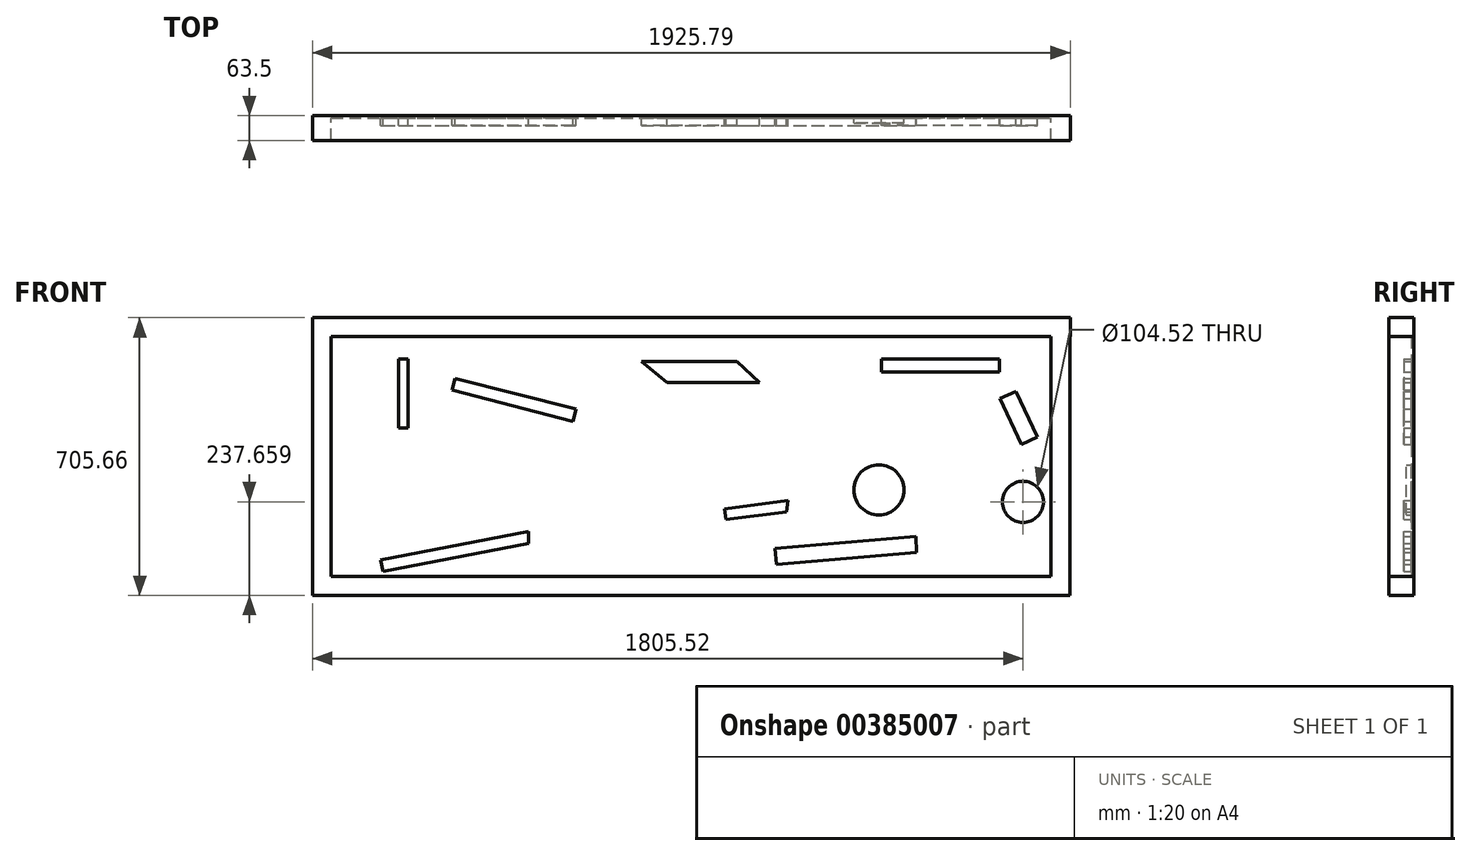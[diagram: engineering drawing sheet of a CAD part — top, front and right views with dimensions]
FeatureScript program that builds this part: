
annotation { "Feature Type Name" : "Feature", "Feature Type Description" : "" }
export const myFeature = defineFeature(function(context is Context, id is Id, definition is map)
    precondition{}
    {
        {
            var Q0;
            Q0=qCreatedBy(makeId("Front.planeOp"),FACE);
            var sketch = newSketch(context, id + "F0", { "sketchPlane" : qUnion([Q0])});
            skLineSegment(sketch, "E0.bottom", {"start": v(-921.13, 198.65) * mm, "end": v(907.67, 198.65) * mm});
            skLineSegment(sketch, "E0.top", {"start": v(-921.13, -410.95) * mm, "end": v(907.67, -410.95) * mm});
            skLineSegment(sketch, "E0.left", {"start": v(-921.13, 198.65) * mm, "end": v(-921.13, -410.95) * mm});
            skLineSegment(sketch, "E0.right", {"start": v(907.67, 198.65) * mm, "end": v(907.67, -410.95) * mm});
            skCircle(sketch, "E1", {"center": v(836.35, -221.32) * mm, "radius": 52.26 * mm});
            skLineSegment(sketch, "E2.bottom", {"start": v(-749.92, 141.95) * mm, "end": v(-725.7, 141.95) * mm});
            skLineSegment(sketch, "E2.top", {"start": v(-749.92, -33.63) * mm, "end": v(-725.7, -33.63) * mm});
            skLineSegment(sketch, "E2.left", {"start": v(-749.92, 141.95) * mm, "end": v(-749.92, -33.63) * mm});
            skLineSegment(sketch, "E2.right", {"start": v(-725.7, 141.95) * mm, "end": v(-725.7, -33.63) * mm});
            skLineSegment(sketch, "E3.bottom", {"start": v(775.8, 141.95) * mm, "end": v(476.1, 141.95) * mm});
            skLineSegment(sketch, "E3.top", {"start": v(775.8, 108.65) * mm, "end": v(476.1, 108.65) * mm});
            skLineSegment(sketch, "E3.left", {"start": v(775.8, 141.95) * mm, "end": v(775.8, 108.65) * mm});
            skLineSegment(sketch, "E3.right", {"start": v(476.1, 141.95) * mm, "end": v(476.1, 108.65) * mm});
            skLineSegment(sketch, "E4", {"start": v(206.69, -339.38) * mm, "end": v(563.9, -309.11) * mm});
            skLineSegment(sketch, "E5", {"start": v(206.69, -339.38) * mm, "end": v(210.17, -380.5) * mm});
            skLineSegment(sketch, "E6", {"start": v(210.17, -380.5) * mm, "end": v(566.06, -350.33) * mm});
            skLineSegment(sketch, "E7", {"start": v(566.06, -350.33) * mm, "end": v(563.9, -309.11) * mm});
            skLineSegment(sketch, "E8", {"start": v(109.81, 135.9) * mm, "end": v(-132.36, 135.9) * mm});
            skLineSegment(sketch, "E9", {"start": v(109.81, 135.9) * mm, "end": v(167.33, 81.4) * mm});
            skLineSegment(sketch, "E10", {"start": v(-132.36, 135.9) * mm, "end": v(-68.8, 81.4) * mm});
            skLineSegment(sketch, "E11", {"start": v(-68.8, 81.4) * mm, "end": v(167.33, 81.4) * mm});
            skLineSegment(sketch, "E12.bottom", {"start": v(-921.13, 198.65) * mm, "end": v(-969.17, 198.65) * mm});
            skLineSegment(sketch, "E12.top", {"start": v(-921.13, -410.95) * mm, "end": v(-969.17, -410.95) * mm});
            skLineSegment(sketch, "E12.right", {"start": v(-969.17, 198.65) * mm, "end": v(-969.17, -410.95) * mm});
            skLineSegment(sketch, "E13.bottom", {"start": v(907.67, 198.65) * mm, "end": v(955.7, 198.65) * mm});
            skLineSegment(sketch, "E13.top", {"start": v(907.67, -410.95) * mm, "end": v(955.7, -410.95) * mm});
            skLineSegment(sketch, "E13.right", {"start": v(955.7, 198.65) * mm, "end": v(955.7, -410.95) * mm});
            skLineSegment(sketch, "E14.bottom", {"start": v(-969.17, -410.95) * mm, "end": v(955.7, -410.95) * mm});
            skLineSegment(sketch, "E15.bottom", {"start": v(-969.17, -410.95) * mm, "end": v(955.73, -410.95) * mm});
            skLineSegment(sketch, "E15.top", {"start": v(-969.17, -458.98) * mm, "end": v(955.73, -458.98) * mm});
            skLineSegment(sketch, "E15.left", {"start": v(-969.17, -410.95) * mm, "end": v(-969.17, -458.98) * mm});
            skLineSegment(sketch, "E15.right", {"start": v(955.73, -410.95) * mm, "end": v(955.73, -458.98) * mm});
            skLineSegment(sketch, "E16.bottom", {"start": v(-969.17, 198.65) * mm, "end": v(956.62, 198.65) * mm});
            skLineSegment(sketch, "E16.top", {"start": v(-969.17, 246.68) * mm, "end": v(956.62, 246.68) * mm});
            skLineSegment(sketch, "E16.left", {"start": v(-969.17, 198.65) * mm, "end": v(-969.17, 246.68) * mm});
            skLineSegment(sketch, "E16.right", {"start": v(956.62, 198.65) * mm, "end": v(956.62, 246.68) * mm});
            skLineSegment(sketch, "E17.bottom", {"start": v(-921.13, -410.95) * mm, "end": v(-31.47, -410.95) * mm});
            skLineSegment(sketch, "E17.left", {"start": v(-921.13, -410.95) * mm, "end": v(-921.13, -371.5) * mm});
            skLineSegment(sketch, "E18", {"start": v(-606.28, 91.49) * mm, "end": v(-299.2, 14.32) * mm});
            skLineSegment(sketch, "E19", {"start": v(-299.2, 14.32) * mm, "end": v(-307.1, -17.17) * mm});
            skLineSegment(sketch, "E20", {"start": v(-307.1, -17.17) * mm, "end": v(-614.07, 62.56) * mm});
            skLineSegment(sketch, "E21", {"start": v(-614.07, 62.56) * mm, "end": v(-606.28, 91.49) * mm});
            skLineSegment(sketch, "E22", {"start": v(81.92, -266.64) * mm, "end": v(235.6, -246.6) * mm});
            skLineSegment(sketch, "E23", {"start": v(81.92, -266.64) * mm, "end": v(78.34, -239.22) * mm});
            skLineSegment(sketch, "E24", {"start": v(78.34, -239.22) * mm, "end": v(239.82, -218.16) * mm});
            skLineSegment(sketch, "E25", {"start": v(239.82, -218.16) * mm, "end": v(235.6, -246.6) * mm});
            skLineSegment(sketch, "E26", {"start": v(-795.26, -368.88) * mm, "end": v(-420.46, -296.43) * mm});
            skLineSegment(sketch, "E27", {"start": v(-795.26, -368.88) * mm, "end": v(-789.58, -398.26) * mm});
            skLineSegment(sketch, "E28", {"start": v(-789.58, -398.26) * mm, "end": v(-420.46, -326.9) * mm});
            skLineSegment(sketch, "E29", {"start": v(-420.46, -326.9) * mm, "end": v(-420.46, -296.43) * mm});
            skLineSegment(sketch, "E30", {"start": v(818.66, 58.8) * mm, "end": v(872.92, -56.8) * mm});
            skLineSegment(sketch, "E31", {"start": v(872.92, -56.8) * mm, "end": v(832.51, -75.76) * mm});
            skLineSegment(sketch, "E32", {"start": v(832.51, -75.76) * mm, "end": v(777.59, 41.28) * mm});
            skLineSegment(sketch, "E33", {"start": v(777.59, 41.28) * mm, "end": v(818.66, 58.8) * mm});
            skCircle(sketch, "E34", {"center": v(470.15, -190.9) * mm, "radius": 63.63 * mm});
            skSolve(sketch);
        }
        {
            var Q0;
            Q0=makeQuery(id+"F0.imprint","IMPRINT",FACE,{"disambiguationData":[TD([[makeQuery(id+"F0.imprint","IMPRINT",EDGE,{"derivedFrom":sQuery(id+"F0.wireOp",EDGE,"E16.top")}),-1.0]])]});
            var Q1;
            {var subQ0=sQuery(id+"F0.wireOp",EDGE,"E12.right");Q1=makeQuery(id+"F0.imprint","IMPRINT",FACE,{"disambiguationData":[TD([[makeQuery(id+"F0.imprint","IMPRINT",EDGE,{"derivedFrom":subQ0}),1.0]])]});}
            var Q2;
            Q2=makeQuery(id+"F0.imprint","IMPRINT",FACE,{"disambiguationData":[TD([[makeQuery(id+"F0.imprint","IMPRINT",EDGE,{"derivedFrom":sQuery(id+"F0.wireOp",EDGE,"E15.top")}),1.0]])]});
            var Q3;
            {var subQ0=sQuery(id+"F0.wireOp",EDGE,"E13.right");Q3=makeQuery(id+"F0.imprint","IMPRINT",FACE,{"disambiguationData":[TD([[makeQuery(id+"F0.imprint","IMPRINT",EDGE,{"derivedFrom":subQ0}),-1.0]])]});}
            extrude(context, id + "F1", {"entities" : qUnion([Q0, Q1, Q2, Q3]), "depth" : 63.5 * mm});
        }
        {
            var Q0;
            {var subQ0=sQuery(id+"F0.wireOp",EDGE,"E0.top");Q0=makeQuery(id+"F0.imprint","IMPRINT",FACE,{"disambiguationData":[TD([[makeQuery(id+"F0.imprint","IMPRINT",EDGE,{"derivedFrom":subQ0}),1.0]])]});}
            extrude(context, id + "F2", {"entities" : qUnion([Q0]), "operationType" : NewBodyOperationType.ADD, "depth" : 6.35 * mm});
        }
        {
            var Q0;
            Q0=qCreatedBy(makeId("Right.planeOp"),FACE);
            var sketch = newSketch(context, id + "F3", { "sketchPlane" : qUnion([Q0])});
            skArc(sketch, "E35", {"start": v(0, 0) * mm, "mid": v(-49.1, -67.34) * mm, "end": v(0, -134.69) * mm});
            skSolve(sketch);
        }
        {
            var Q0;
            Q0=sQuery(id+"F3.wireOp",EDGE,"E35");
            extrude(context, id + "F4", {"bodyType" : ToolBodyType.SURFACE, "surfaceEntities" : qUnion([Q0]), "depth" : 152.4 * mm, "hasSecondDirection" : true, "secondDirectionOppositeDirection" : true, "secondDirectionDepth" : 177.8 * mm});
        }
        {
            var Q0;
            Q0=makeQuery(id+"F0.imprint","IMPRINT",FACE,{"disambiguationData":[TD([[makeQuery(id+"F0.imprint","IMPRINT",EDGE,{"derivedFrom":sQuery(id+"F0.wireOp",EDGE,"E3.bottom")}),1.0]])]});
            var Q1;
            Q1=makeQuery(id+"F0.imprint","IMPRINT",FACE,{"disambiguationData":[TD([[makeQuery(id+"F0.imprint","IMPRINT",EDGE,{"derivedFrom":sQuery(id+"F0.wireOp",EDGE,"E8")}),1.0]])]});
            var Q2;
            Q2=makeQuery(id+"F0.imprint","IMPRINT",FACE,{"disambiguationData":[TD([[makeQuery(id+"F0.imprint","IMPRINT",EDGE,{"derivedFrom":sQuery(id+"F0.wireOp",EDGE,"E18")}),-1.0]])]});
            var Q3;
            Q3=makeQuery(id+"F0.imprint","IMPRINT",FACE,{"disambiguationData":[TD([[makeQuery(id+"F0.imprint","IMPRINT",EDGE,{"derivedFrom":sQuery(id+"F0.wireOp",EDGE,"E26")}),-1.0]])]});
            var Q4;
            Q4=makeQuery(id+"F0.imprint","IMPRINT",FACE,{"disambiguationData":[TD([[makeQuery(id+"F0.imprint","IMPRINT",EDGE,{"derivedFrom":sQuery(id+"F0.wireOp",EDGE,"E22")}),1.0]])]});
            var Q5;
            Q5=makeQuery(id+"F0.imprint","IMPRINT",FACE,{"disambiguationData":[TD([[makeQuery(id+"F0.imprint","IMPRINT",EDGE,{"derivedFrom":sQuery(id+"F0.wireOp",EDGE,"E4")}),-1.0]])]});
            var Q6;
            Q6=makeQuery(id+"F0.imprint","IMPRINT",FACE,{"disambiguationData":[TD([[makeQuery(id+"F0.imprint","IMPRINT",EDGE,{"derivedFrom":sQuery(id+"F0.wireOp",EDGE,"E2.bottom")}),-1.0]])]});
            var Q7;
            Q7=makeQuery(id+"F0.imprint","IMPRINT",FACE,{"disambiguationData":[TD([[makeQuery(id+"F0.imprint","IMPRINT",EDGE,{"derivedFrom":sQuery(id+"F0.wireOp",EDGE,"E30")}),-1.0]])]});
            extrude(context, id + "F5", {"entities" : qUnion([Q0, Q1, Q2, Q3, Q4, Q5, Q6, Q7]), "operationType" : NewBodyOperationType.ADD, "depth" : 25.4 * mm});
        }
        {
            var Q0;
            Q0=makeQuery(id+"F0.imprint","IMPRINT",FACE,{"disambiguationData":[TD([[makeQuery(id+"F0.imprint","IMPRINT",EDGE,{"derivedFrom":sQuery(id+"F0.wireOp",EDGE,"E34")}),1.0]])]});
            extrude(context, id + "F6", {"entities" : qUnion([Q0]), "operationType" : NewBodyOperationType.ADD, "depth" : 19.05 * mm});
        }
    });
